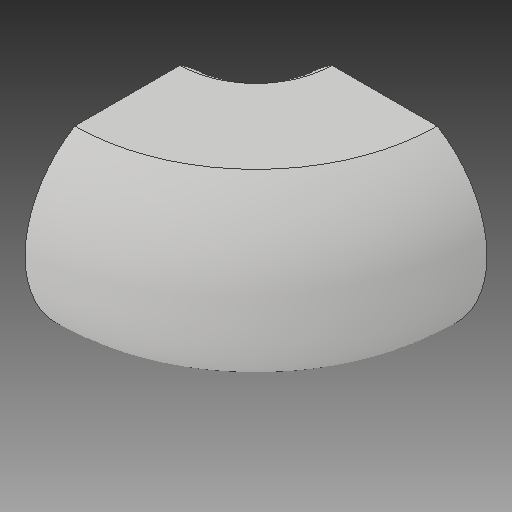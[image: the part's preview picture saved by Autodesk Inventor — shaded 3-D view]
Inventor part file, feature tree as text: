
AUTODESK INVENTOR PART (.ipt)
format: ipt  version: 2017 (Build 210142000, 142)  size: 137,216 bytes
history: native  units: in
note: dims shown in document units (in); Inventor stores cm internally (conversion verified against a paired STEP export)
features: other x1, delete_face x1, sketch x1
ambient origin geometry x8: Origin, YZ Plane, XZ Plane, XY Plane, X Axis, Y Axis, Z Axis, Center Point
bodies: Solid1 (feature_tree)
feature tree (3):
  other  "corridor"
  delete_face  "Delete Face2"
  sketch  "Sketch1"  dims[d1=4.0in d2=90.0deg d28=45.0deg d31=3.8873in]
